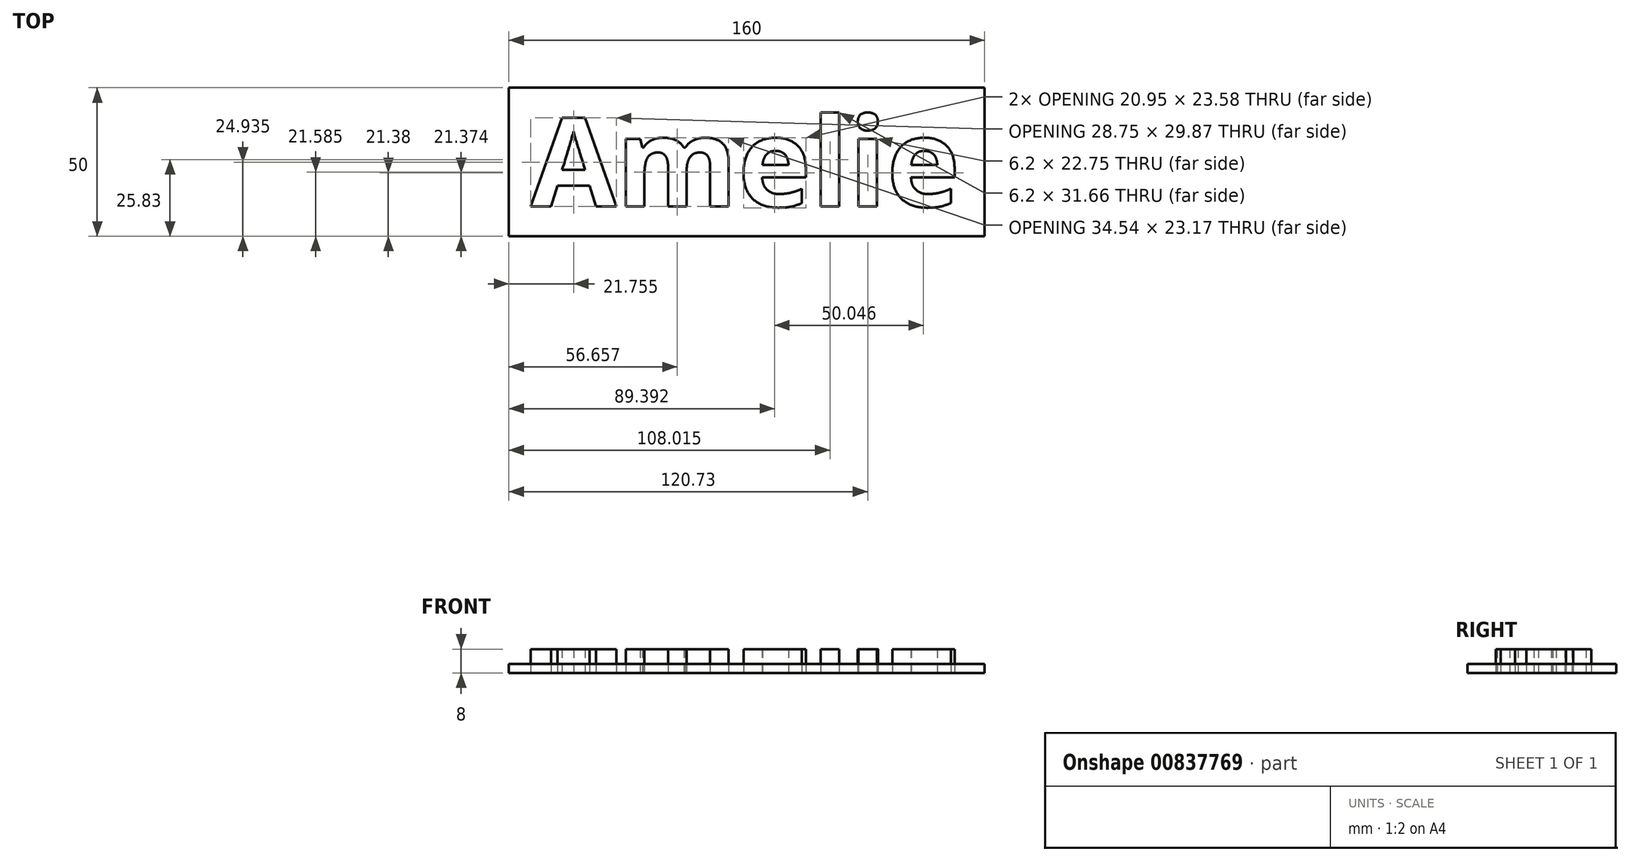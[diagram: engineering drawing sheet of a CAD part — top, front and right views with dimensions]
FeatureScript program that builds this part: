
annotation { "Feature Type Name" : "Feature", "Feature Type Description" : "" }
export const myFeature = defineFeature(function(context is Context, id is Id, definition is map)
    precondition{}
    {
        {
            var Q0;
            Q0=qCreatedBy(makeId("Top.planeOp"),FACE);
            var sketch = newSketch(context, id + "F0", { "sketchPlane" : qUnion([Q0])});
            skLineSegment(sketch, "E0.bottom", {"start": v(80, -25) * mm, "end": v(-80, -25) * mm});
            skLineSegment(sketch, "E0.top", {"start": v(80, 25) * mm, "end": v(-80, 25) * mm});
            skLineSegment(sketch, "E0.left", {"start": v(80, -25) * mm, "end": v(80, 25) * mm});
            skLineSegment(sketch, "E0.right", {"start": v(-80, -25) * mm, "end": v(-80, 25) * mm});
            skPoint(sketch, "E0.middle", {"position": v(0, 0) * mm});
            skText(sketch, "E1", { "text": "Amelie", "fontName": "OpenSans-Bold.ttf"});
            const initialGuessF0  = {"E1": [-0.07262, -0.015, 1, 0, 0.03]};
            skSetInitialGuess(sketch, initialGuessF0);
            skSolve(sketch);
        }
        {
            var Q0;
            Q0=makeQuery(id+"F0.imprint","IMPRINT",FACE,{"disambiguationData":[TD([[makeQuery(id+"F0.imprint","IMPRINT",EDGE,{"derivedFrom":sQuery(id+"F0.wireOp",EDGE,"E1.sketch_text.stroke-0")}),-1.0]])]});
            var Q1;
            Q1=makeQuery(id+"F0.imprint","IMPRINT",FACE,{"disambiguationData":[TD([[makeQuery(id+"F0.imprint","IMPRINT",EDGE,{"derivedFrom":sQuery(id+"F0.wireOp",EDGE,"E1.sketch_text.stroke-12")}),-1.0]])]});
            var Q2;
            Q2=makeQuery(id+"F0.imprint","IMPRINT",FACE,{"disambiguationData":[TD([[makeQuery(id+"F0.imprint","IMPRINT",EDGE,{"derivedFrom":sQuery(id+"F0.wireOp",EDGE,"E1.sketch_text.stroke-40")}),-1.0]])]});
            var Q3;
            Q3=makeQuery(id+"F0.imprint","IMPRINT",FACE,{"disambiguationData":[TD([[makeQuery(id+"F0.imprint","IMPRINT",EDGE,{"derivedFrom":sQuery(id+"F0.wireOp",EDGE,"E1.sketch_text.stroke-60")}),-1.0]])]});
            var Q4;
            Q4=makeQuery(id+"F0.imprint","IMPRINT",FACE,{"disambiguationData":[TD([[makeQuery(id+"F0.imprint","IMPRINT",EDGE,{"derivedFrom":sQuery(id+"F0.wireOp",EDGE,"E1.sketch_text.stroke-69")}),-1.0]])]});
            var Q5;
            Q5=makeQuery(id+"F0.imprint","IMPRINT",FACE,{"disambiguationData":[TD([[makeQuery(id+"F0.imprint","IMPRINT",EDGE,{"derivedFrom":sQuery(id+"F0.wireOp",EDGE,"E1.sketch_text.stroke-64")}),-1.0]])]});
            var Q6;
            Q6=makeQuery(id+"F0.imprint","IMPRINT",FACE,{"disambiguationData":[TD([[makeQuery(id+"F0.imprint","IMPRINT",EDGE,{"derivedFrom":sQuery(id+"F0.wireOp",EDGE,"E1.sketch_text.stroke-73")}),-1.0]])]});
            extrude(context, id + "F1", {"entities" : qUnion([Q0, Q1, Q2, Q3, Q4, Q5, Q6]), "depth" : 8 * mm, "offsetDistance" : 25 * mm});
        }
        {
            var Q0;
            Q0=makeQuery(id+"F0.imprint","IMPRINT",FACE,{"disambiguationData":[TD([[makeQuery(id+"F0.imprint","IMPRINT",EDGE,{"derivedFrom":sQuery(id+"F0.wireOp",EDGE,"E0.bottom")}),-1.0]])]});
            var Q1;
            Q1=makeQuery(id+"F0.imprint","IMPRINT",FACE,{"disambiguationData":[TD([[makeQuery(id+"F0.imprint","IMPRINT",EDGE,{"derivedFrom":sQuery(id+"F0.wireOp",EDGE,"E1.sketch_text.stroke-8")}),1.0]])]});
            var Q2;
            Q2=makeQuery(id+"F0.imprint","IMPRINT",FACE,{"disambiguationData":[TD([[makeQuery(id+"F0.imprint","IMPRINT",EDGE,{"derivedFrom":sQuery(id+"F0.wireOp",EDGE,"E1.sketch_text.stroke-40")}),1.0]])]});
            var Q3;
            Q3=makeQuery(id+"F0.imprint","IMPRINT",FACE,{"disambiguationData":[TD([[makeQuery(id+"F0.imprint","IMPRINT",EDGE,{"derivedFrom":sQuery(id+"F0.wireOp",EDGE,"E1.sketch_text.stroke-73")}),1.0]])]});
            extrude(context, id + "F2", {"entities" : qUnion([Q0, Q1, Q2, Q3]), "depth" : 3 * mm, "offsetDistance" : 25 * mm});
        }
    });
